SOLIDWORKS PART (.sldprt)
format: sldprt  version: not decoded by parser v0  size: 250,880 bytes
history: native  units: mm
features: sketch x6, cut_extrude x4, plane x3, extrude x2, chamfer x2, material x1, fillet x1, pattern_linear x1 (+8 scaffold rows collapsed)
feature tree (28):
  scaffold x8  (default folders/planes/origin — collapsed)
  material  "Matériau <non spécifié>"
  plane  "Face"
  plane  "Dessus"
  plane  "Droite"
  sketch  "Esquisse1"  dims[D1=5.0mm D2=7.55mm]
  extrude  "Extrusion1"  Depth=10.02mm
  chamfer  "Chanfrein1"  Distance=3.55mm Angle=25deg
  sketch  "Esquisse2"  dims[D1=3.45mm]
  cut_extrude  "Enlèv. mat.-Extru.1"  Depth=1mm
  sketch  "Esquisse3"  dims[c1.D1=5.0mm c1.D2=4.0mm c1.D3=0.8mm c1.D4=0.67mm c2.D3=0.8mm c2.D4=0.9mm c3.D3=0.8mm c3.D4=0.5mm]
  cut_extrude  "Enlèv. mat.-Extru.2"  Depth=1.6mm
  sketch  "Esquisse4"  dims[D1=2.5mm D2=2.5mm]
  cut_extrude  "Enlèv. mat.-Extru.3"  Depth=1.6mm
  sketch  "Esquisse5"  dims[D1=~0.52123mm D2=5.2mm]
  extrude  "Extrusion2"  Depth=5mm
  fillet  "Congé1"  Radius=0.5mm
  sketch  "Esquisse6"  dims[D1=0.4mm D2=0.8mm D3=1.6mm D4=3.2mm]
  cut_extrude  "Enlèv. mat.-Extru.4"  Depth=0.5mm
  pattern_linear  "Répétition linéaire5"  Count1=3 Count2=1 Spacing1=5mm Spacing2=50mm
  chamfer  "Chanfrein2"  Distance=3.55mm Angle=25deg
decode coverage: 16 of 16 modeling features carry decoded parameters
note: ~ marks probable driven/reference dimensions
note: suppression state not decoded; provenance and decode notes live in map.json
